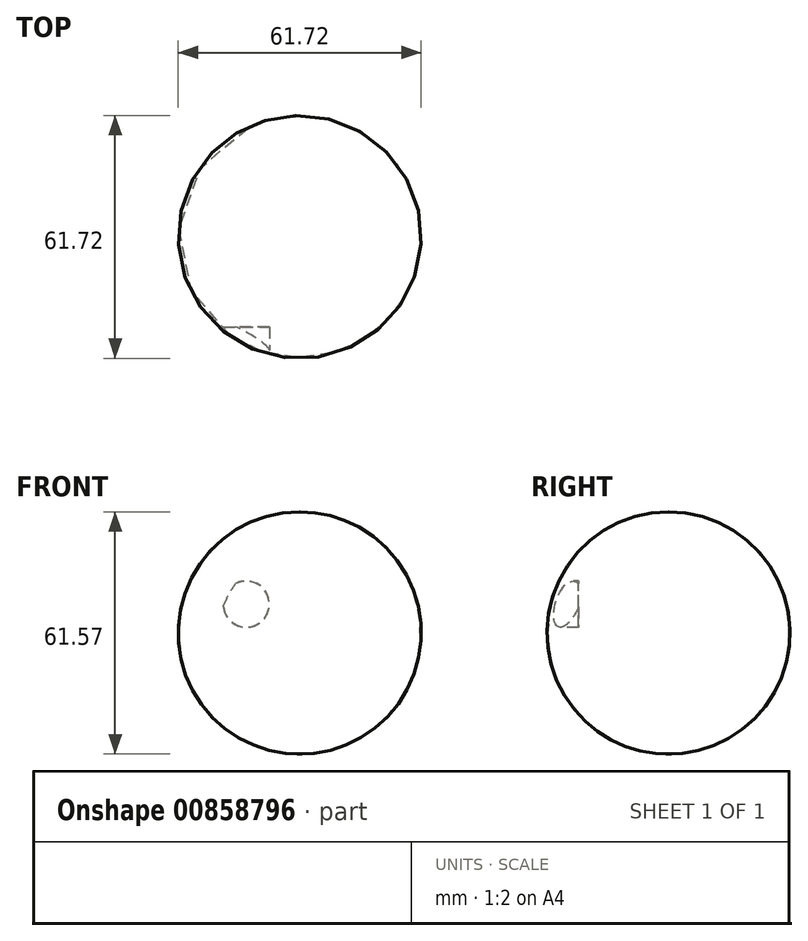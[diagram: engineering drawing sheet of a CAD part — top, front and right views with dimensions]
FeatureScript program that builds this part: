
annotation { "Feature Type Name" : "Feature", "Feature Type Description" : "" }
export const myFeature = defineFeature(function(context is Context, id is Id, definition is map)
    precondition{}
    {
        {
            var Q0;
            Q0=qCreatedBy(makeId("Front.planeOp"),FACE);
            var sketch = newSketch(context, id + "F0", { "sketchPlane" : qUnion([Q0])});
            skLineSegment(sketch, "E0", {"start": v(0, 0) * mm, "end": v(0, 61.57) * mm});
            skArc(sketch, "E1", {"start": v(0, 0) * mm, "mid": v(30.7, 30.78) * mm, "end": v(0, 61.57) * mm});
            skSolve(sketch);
        }
        {
            var Q0;
            Q0=makeQuery(id+"F0.imprint","IMPRINT",FACE,{"disambiguationData":[TD([[makeQuery(id+"F0.imprint","IMPRINT",EDGE,{"derivedFrom":sQuery(id+"F0.wireOp",EDGE,"E0")}),-1.0]])]});
            var Q1;
            Q1=sQuery(id+"F0.wireOp",EDGE,"E0");
            revolve(context, id + "F1", {"surfaceOperationType" : NewSurfaceOperationType.NEW, "entities" : qUnion([Q0]), "axis" : qUnion([Q1]), "revolveType" : RevolveType.FULL});
        }
        {
            var Q0;
            Q0=qCreatedBy(makeId("Front.planeOp"),FACE);
            cPlane(context, id + "F2", {"entities" : qUnion([Q0]), "cplaneType" : CPlaneType.OFFSET, "offset" : 38.1 * mm, "width" : 152.4 * mm, "height" : 152.4 * mm});
        }
        {
            var Q0;
            Q0=qCreatedBy(id+"F2.planeOp",FACE);
            var sketch = newSketch(context, id + "F3", { "sketchPlane" : qUnion([Q0])});
            skCircle(sketch, "E2", {"center": v(-13.56, 38.1) * mm, "radius": 5.86 * mm});
            skCircle(sketch, "E3.MirrorC", {"center": v(13.56, 38.1) * mm, "radius": 5.86 * mm});
            skSolve(sketch);
        }
        {
            var Q0;
            Q0=makeQuery(id+"F3.imprint","IMPRINT",FACE,{"disambiguationData":[TD([[makeQuery(id+"F3.imprint","IMPRINT",EDGE,{"derivedFrom":sQuery(id+"F3.wireOp",EDGE,"E2")}),1.0]])]});
            var Q1;
            Q1=makeQuery(id+"F3.imprint","IMPRINT",FACE,{"disambiguationData":[TD([[makeQuery(id+"F3.imprint","IMPRINT",EDGE,{"derivedFrom":sQuery(id+"F3.wireOp",EDGE,"E3.MirrorC")}),-1.0]])]});
            extrude(context, id + "F4", {"entities" : qUnion([Q0, Q1]), "operationType" : NewBodyOperationType.REMOVE, "oppositeDirection" : true, "depth" : 15.24 * mm, "offsetDistance" : 25.4 * mm});
        }
    });
